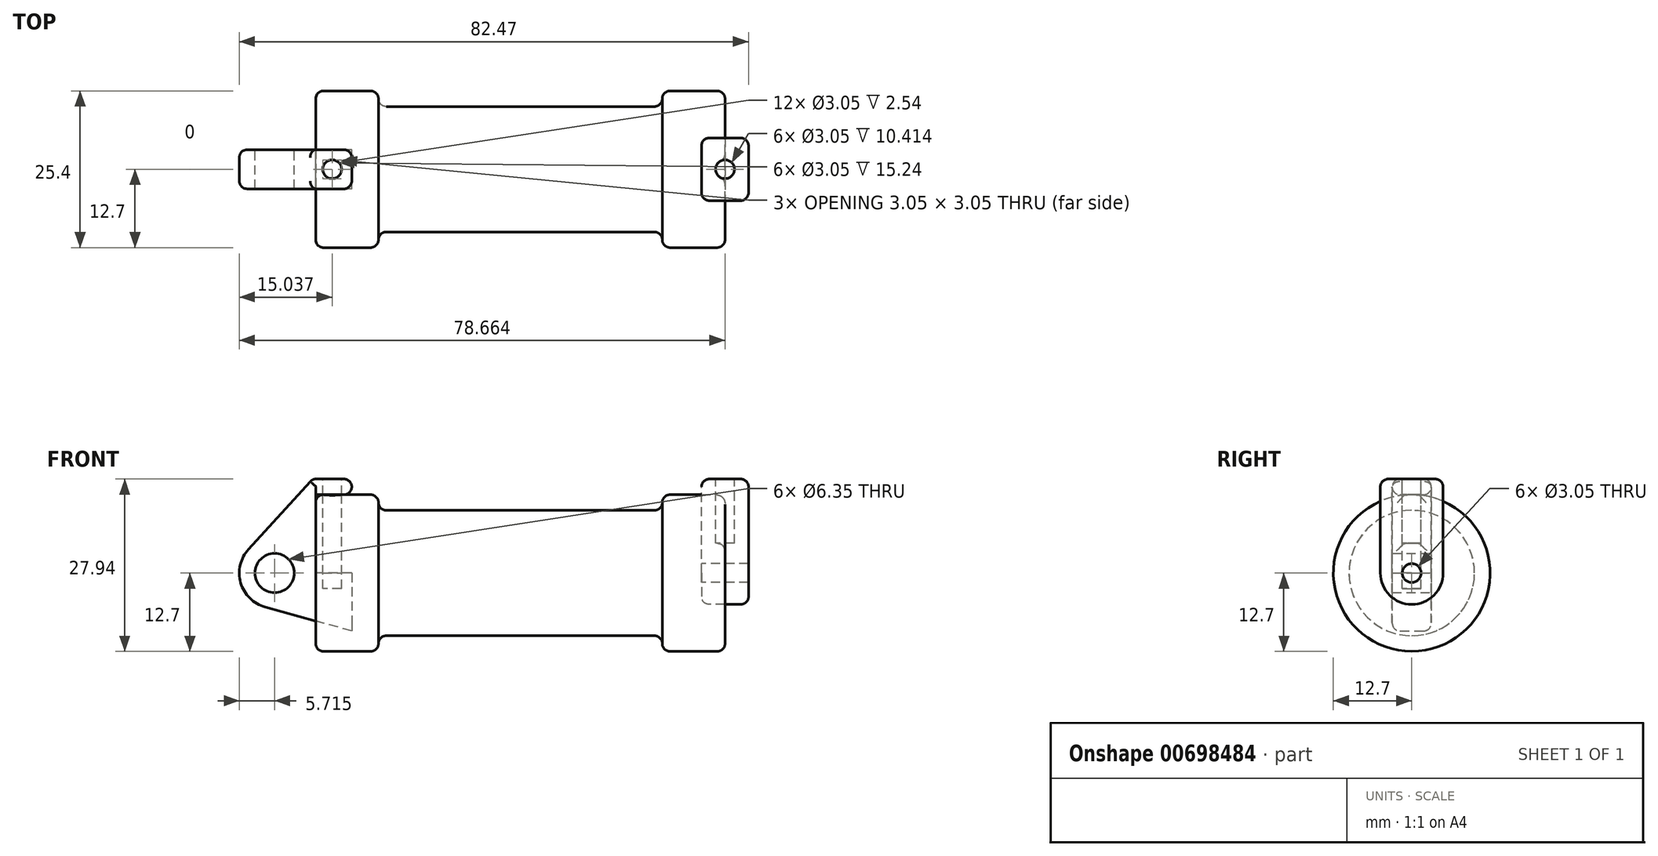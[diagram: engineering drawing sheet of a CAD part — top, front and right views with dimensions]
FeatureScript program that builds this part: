
annotation { "Feature Type Name" : "Feature", "Feature Type Description" : "" }
export const myFeature = defineFeature(function(context is Context, id is Id, definition is map)
    precondition{}
    {
        {
            var Q0;
            Q0=qCreatedBy(makeId("Front.planeOp"),FACE);
            var sketch = newSketch(context, id + "F0", { "sketchPlane" : qUnion([Q0])});
            skLineSegment(sketch, "E0", {"start": v(0, 0) * mm, "end": v(0, 12.7) * mm});
            skLineSegment(sketch, "E1", {"start": v(0, 12.7) * mm, "end": v(10.16, 12.7) * mm});
            skLineSegment(sketch, "E2", {"start": v(10.16, 12.7) * mm, "end": v(10.16, 10.16) * mm});
            skLineSegment(sketch, "E3", {"start": v(10.16, 10.16) * mm, "end": v(56.13, 10.16) * mm});
            skLineSegment(sketch, "E4", {"start": v(56.13, 10.16) * mm, "end": v(56.13, 12.7) * mm});
            skLineSegment(sketch, "E5", {"start": v(56.13, 12.7) * mm, "end": v(66.3, 12.7) * mm});
            skLineSegment(sketch, "E6", {"start": v(66.3, 12.7) * mm, "end": v(66.3, 0) * mm});
            skLineSegment(sketch, "E7", {"start": v(66.3, 0) * mm, "end": v(0, 0) * mm});
            skLineSegment(sketch, "E8", {"start": v(5.84, 15.24) * mm, "end": v(-0.5, 15.24) * mm});
            skLineSegment(sketch, "E9", {"start": v(-0.5, 15.24) * mm, "end": v(-10.88, 3.85) * mm});
            skLineSegment(sketch, "E10", {"start": v(0, 0) * mm, "end": v(-6.65, 0) * mm});
            skCircle(sketch, "E11", {"center": v(-6.65, 0) * mm, "radius": 5.72 * mm});
            skCircle(sketch, "E12", {"center": v(-6.65, 0) * mm, "radius": 3.18 * mm});
            skLineSegment(sketch, "E13", {"start": v(5.84, 15.24) * mm, "end": v(5.84, -9.4) * mm});
            skLineSegment(sketch, "E14", {"start": v(5.84, -9.4) * mm, "end": v(-8.18, -5.5) * mm});
            skSolve(sketch);
        }
        {
            var Q0;
            {var subQ1=sQuery(id+"F0.wireOp",EDGE,"E0");Q0=makeQuery(id+"F0.imprint","IMPRINT",FACE,{"disambiguationData":[TD([[makeQuery(id+"F0.imprint","IMPRINT",EDGE,{"derivedFrom":subQ1}),1.0]])]});}
            var Q1;
            {var subQ0=sQuery(id+"F0.wireOp",EDGE,"E14");Q1=makeQuery(id+"F0.imprint","IMPRINT",FACE,{"disambiguationData":[TD([[makeQuery(id+"F0.imprint","IMPRINT",EDGE,{"derivedFrom":subQ0}),-1.0]])]});}
            var Q2;
            {var subQ5=sQuery(id+"F0.wireOp",EDGE,"E12");Q2=makeQuery(id+"F0.imprint","IMPRINT",FACE,{"disambiguationData":[TD([[makeQuery(id+"F0.imprint","IMPRINT",EDGE,{"derivedFrom":subQ5}),-1.0]])]});}
            extrude(context, id + "F1", {"entities" : qUnion([Q0, Q1, Q2]), "endBound" : BoundingType.SYMMETRIC, "depth" : 6.35 * mm, "offsetDistance" : 25.4 * mm});
        }
        {
            var Q0;
            {var subQ0=sQuery(id+"F0.wireOp",EDGE,"E2");Q0=makeQuery(id+"F0.imprint","IMPRINT",FACE,{"disambiguationData":[TD([[makeQuery(id+"F0.imprint","IMPRINT",EDGE,{"derivedFrom":subQ0}),-1.0]])]});}
            var Q1;
            {var subQ0=sQuery(id+"F0.wireOp",EDGE,"E0");Q1=makeQuery(id+"F0.imprint","IMPRINT",FACE,{"disambiguationData":[TD([[makeQuery(id+"F0.imprint","IMPRINT",EDGE,{"derivedFrom":subQ0}),-1.0]])]});}
            var Q2;
            Q2=sQuery(id+"F0.wireOp",EDGE,"E7");
            revolve(context, id + "F2", {"entities" : qUnion([Q0, Q1]), "axis" : qUnion([Q2]), "revolveType" : RevolveType.FULL});
        }
        {
            var Q0;
            Q0=makeQuery(id+"F2.opRevolve","SWEPT_FACE",FACE,{"disambiguationData":[OSD([sQuery(id+"F0.wireOp",EDGE,"E6")])]});
            var sketch = newSketch(context, id + "F3", { "sketchPlane" : qUnion([Q0])});
            skCircle(sketch, "E15", {"center": v(0, 0) * mm, "radius": 1.52 * mm});
            skCircle(sketch, "E16", {"center": v(0, 0) * mm, "radius": 5.08 * mm});
            skLineSegment(sketch, "E17", {"start": v(5.08, 0) * mm, "end": v(5.08, 15.24) * mm});
            skLineSegment(sketch, "E18", {"start": v(-5.08, 0) * mm, "end": v(-5.08, 15.24) * mm});
            skLineSegment(sketch, "E19", {"start": v(-5.08, 15.24) * mm, "end": v(5.08, 15.24) * mm});
            skSolve(sketch);
        }
        {
            var Q0;
            Q0=makeQuery(id+"F3.imprint","IMPRINT",FACE,{"disambiguationData":[TD([[makeQuery(id+"F3.imprint","IMPRINT",EDGE,{"derivedFrom":sQuery(id+"F3.wireOp",EDGE,"E15")}),-1.0]])]});
            var Q1;
            {var subQ0=sQuery(id+"F3.wireOp",EDGE,"E17");var subQ1=sQuery(id+"F3.wireOp",EDGE,"E16");var subQ2=makeQuery(id+"F3.imprint","INTERSECT",VERTEX,{"derivedFrom":[subQ1,subQ0]});Q1=makeQuery(id+"F3.imprint","IMPRINT",FACE,{"disambiguationData":[TD([[makeQuery(id+"F3.imprint","IMPRINT",EDGE,{"disambiguationData":[TD([[subQ2,-1.0]])],"derivedFrom":subQ1}),-1.0]])]});}
            var Q2;
            {var subQ0=sQuery(id+"F3.wireOp",EDGE,"E19");Q2=makeQuery(id+"F3.imprint","IMPRINT",FACE,{"disambiguationData":[TD([[makeQuery(id+"F3.imprint","IMPRINT",EDGE,{"derivedFrom":subQ0}),-1.0]])]});}
            extrude(context, id + "F4", {"entities" : qUnion([Q0, Q1, Q2]), "endBound" : BoundingType.SYMMETRIC, "depth" : 7.62 * mm, "offsetDistance" : 25.4 * mm});
        }
        {
            var Q0;
            Q0=makeQuery(id+"F4.opExtrude","SWEPT_FACE",FACE,{"disambiguationData":[OSD([sQuery(id+"F3.wireOp",EDGE,"E19")])]});
            var sketch = newSketch(context, id + "F5", { "sketchPlane" : qUnion([Q0])});
            skLineSegment(sketch, "E20", {"start": v(-0.5, 3.18) * mm, "end": v(5.84, -3.18) * mm, "construction": true});
            skCircle(sketch, "E21", {"center": v(2.67, 0) * mm, "radius": 1.52 * mm});
            skLineSegment(sketch, "E22", {"start": v(70.1, 5.08) * mm, "end": v(62.48, -5.08) * mm, "construction": true});
            skCircle(sketch, "E23", {"center": v(66.3, 0) * mm, "radius": 1.52 * mm});
            skSolve(sketch);
        }
        {
            var Q0;
            Q0=makeQuery(id+"F5.imprint","IMPRINT",FACE,{"disambiguationData":[TD([[makeQuery(id+"F5.imprint","IMPRINT",EDGE,{"derivedFrom":sQuery(id+"F5.wireOp",EDGE,"E23")}),1.0]])]});
            var Q1;
            Q1=sQuery(id+"F5.wireOp",EDGE,"E21");
            var Q2;
            Q2=sQuery(id+"F5.wireOp",EDGE,"E23");
            extrude(context, id + "F6", {"entities" : qUnion([Q0]), "operationType" : NewBodyOperationType.REMOVE, "surfaceEntities" : qUnion([Q1, Q2]), "oppositeDirection" : true, "depth" : 10.4 * mm, "offsetDistance" : 25.4 * mm});
        }
        {
            var Q0;
            Q0=makeQuery(id+"F5.imprint","IMPRINT",FACE,{"disambiguationData":[TD([[makeQuery(id+"F5.imprint","IMPRINT",EDGE,{"derivedFrom":sQuery(id+"F5.wireOp",EDGE,"E21")}),1.0]])]});
            extrude(context, id + "F7", {"entities" : qUnion([Q0]), "operationType" : NewBodyOperationType.REMOVE, "oppositeDirection" : true, "depth" : 17.78 * mm, "offsetDistance" : 25.4 * mm});
        }
        {
            var Q0;
            Q0=makeQuery(id+"F2.opRevolve","SWEPT_FACE",FACE,{"disambiguationData":[OSD([sQuery(id+"F0.wireOp",EDGE,"E2")])]});
            var Q1;
            Q1=makeQuery(id+"F2.opRevolve","SWEPT_FACE",FACE,{"disambiguationData":[OSD([sQuery(id+"F0.wireOp",EDGE,"E4")])]});
            fillet(context, id + "F8", {"entities" : qUnion([Q0, Q1]), "radius" : 1.27 * mm, "tangentPropagation" : true, "allowEdgeOverflow" : false});
        }
        {
            var Q0;
            Q0=makeQuery(id+"F1.opExtrude","CAP_EDGE",EDGE,{"disambiguationData":[OSD([sQuery(id+"F0.wireOp",EDGE,"E8")])],"isStart":false});
            var Q1;
            Q1=makeQuery(id+"F1.opExtrude","SWEPT_EDGE",EDGE,{"disambiguationData":[OSD([sQuery(id+"F0.wireOp",EDGE,"E8"),sQuery(id+"F0.wireOp",EDGE,"E9")])]});
            var Q2;
            Q2=makeQuery(id+"F1.opExtrude","CAP_EDGE",EDGE,{"disambiguationData":[OSD([sQuery(id+"F0.wireOp",EDGE,"E8")])],"isStart":true});
            fillet(context, id + "F9", {"entities" : qUnion([Q0, Q1, Q2]), "radius" : 1.27 * mm, "tangentPropagation" : true, "allowEdgeOverflow" : false});
        }
        {
            var Q0;
            Q0=makeQuery(id+"F1.opExtrude","SWEPT_EDGE",EDGE,{"disambiguationData":[OSD([sQuery(id+"F0.wireOp",EDGE,"E8"),sQuery(id+"F0.wireOp",EDGE,"E13")])]});
            var Q1;
            Q1=makeQuery(id+"F1.opExtrude","CAP_EDGE",EDGE,{"disambiguationData":[OSD([sQuery(id+"F0.wireOp",EDGE,"E9")])],"isStart":true});
            var Q2;
            Q2=makeQuery(id+"F1.opExtrude","CAP_EDGE",EDGE,{"disambiguationData":[OSD([sQuery(id+"F0.wireOp",EDGE,"E9")])],"isStart":false});
            var Q3;
            {var subQ0=sQuery(id+"F0.wireOp",EDGE,"E9");Q3=makeQuery(id+"F9.opFillet","BLEND_EDGE",EDGE,{"blendedFrom":[makeQuery(id+"F1.opExtrude","SWEPT_EDGE",EDGE,{"disambiguationData":[OSD([sQuery(id+"F0.wireOp",EDGE,"E8"),subQ0])]}),makeQuery(id+"F1.opExtrude","SWEPT_FACE",FACE,{"disambiguationData":[OSD([subQ0])]})],"blendedInto":[makeQuery(id+"F1.opExtrude","SWEPT_FACE",FACE,{"disambiguationData":[OSD([subQ0])]})]});}
            var Q4;
            Q4=makeQuery(id+"F1.opExtrude","SWEPT_EDGE",EDGE,{"disambiguationData":[OSD([sQuery(id+"F0.wireOp",EDGE,"E9"),sQuery(id+"F0.wireOp",EDGE,"E11")])]});
            var Q5;
            {var subQ0=sQuery(id+"F0.wireOp",EDGE,"E5");Q5=makeQuery(id+"F8.opFillet","BLEND_EDGE",EDGE,{"blendedFrom":[makeQuery(id+"F2.opRevolve","SWEPT_EDGE",EDGE,{"disambiguationData":[OSD([sQuery(id+"F0.wireOp",EDGE,"E4"),subQ0])]}),makeQuery(id+"F2.opRevolve","SWEPT_FACE",FACE,{"disambiguationData":[OSD([subQ0])]})],"blendedInto":[makeQuery(id+"F2.opRevolve","SWEPT_FACE",FACE,{"disambiguationData":[OSD([subQ0])]})]});}
            var Q6;
            Q6=makeQuery(id+"F4.opExtrude","SWEPT_EDGE",EDGE,{"disambiguationData":[OSD([sQuery(id+"F3.wireOp",EDGE,"E17"),sQuery(id+"F3.wireOp",EDGE,"E19")])]});
            var Q7;
            Q7=makeQuery(id+"F4.opExtrude","SWEPT_EDGE",EDGE,{"disambiguationData":[OSD([sQuery(id+"F3.wireOp",EDGE,"E18"),sQuery(id+"F3.wireOp",EDGE,"E19")])]});
            var Q8;
            Q8=makeQuery(id+"F4.opExtrude","CAP_EDGE",EDGE,{"disambiguationData":[OSD([sQuery(id+"F3.wireOp",EDGE,"E19")])],"isStart":false});
            var Q9;
            Q9=makeQuery(id+"F4.opExtrude","CAP_EDGE",EDGE,{"disambiguationData":[OSD([sQuery(id+"F3.wireOp",EDGE,"E19")])],"isStart":true});
            var Q10;
            {var subQ0=sQuery(id+"F0.wireOp",EDGE,"E4");Q10=makeQuery(id+"F8.opFillet","BLEND_EDGE",EDGE,{"blendedFrom":[makeQuery(id+"F2.opRevolve","SWEPT_EDGE",EDGE,{"disambiguationData":[OSD([sQuery(id+"F0.wireOp",EDGE,"E3"),subQ0])]}),makeQuery(id+"F2.opRevolve","SWEPT_EDGE",EDGE,{"disambiguationData":[OSD([subQ0,sQuery(id+"F0.wireOp",EDGE,"E5")])]})],"blendedInto":[]});}
            var Q11;
            {var subQ0=sQuery(id+"F0.wireOp",EDGE,"E3");Q11=makeQuery(id+"F8.opFillet","BLEND_EDGE",EDGE,{"blendedFrom":[makeQuery(id+"F2.opRevolve","SWEPT_EDGE",EDGE,{"disambiguationData":[OSD([subQ0,sQuery(id+"F0.wireOp",EDGE,"E4")])]}),makeQuery(id+"F2.opRevolve","SWEPT_FACE",FACE,{"disambiguationData":[OSD([subQ0])]})],"blendedInto":[makeQuery(id+"F2.opRevolve","SWEPT_FACE",FACE,{"disambiguationData":[OSD([subQ0])]})]});}
            var Q12;
            {var subQ0=sQuery(id+"F0.wireOp",EDGE,"E1");Q12=makeQuery(id+"F8.opFillet","BLEND_EDGE",EDGE,{"blendedFrom":[makeQuery(id+"F2.opRevolve","SWEPT_EDGE",EDGE,{"disambiguationData":[OSD([subQ0,sQuery(id+"F0.wireOp",EDGE,"E2")])]}),makeQuery(id+"F2.opRevolve","SWEPT_FACE",FACE,{"disambiguationData":[OSD([subQ0])]})],"blendedInto":[makeQuery(id+"F2.opRevolve","SWEPT_FACE",FACE,{"disambiguationData":[OSD([subQ0])]})]});}
            fillet(context, id + "F10", {"entities" : qUnion([Q0, Q1, Q2, Q3, Q4, Q5, Q6, Q7, Q8, Q9, Q10, Q11, Q12]), "radius" : 1.27 * mm, "tangentPropagation" : true, "allowEdgeOverflow" : false});
        }
        {
            var Q0;
            {var subQ0=sQuery(id+"F3.wireOp",EDGE,"E19");Q0=makeQuery(id+"F10.opFillet","BLEND_EDGE",EDGE,{"blendedFrom":[makeQuery(id+"F4.opExtrude","CAP_EDGE",EDGE,{"disambiguationData":[OSD([subQ0])],"isStart":false}),makeQuery(id+"F4.opExtrude","SWEPT_FACE",FACE,{"disambiguationData":[OSD([subQ0])]})],"blendedInto":[makeQuery(id+"F4.opExtrude","SWEPT_FACE",FACE,{"disambiguationData":[OSD([subQ0])]})]});}
            var Q1;
            {var subQ0=sQuery(id+"F3.wireOp",EDGE,"E19");Q1=makeQuery(id+"F10.opFillet","BLEND_EDGE",EDGE,{"blendedFrom":[makeQuery(id+"F4.opExtrude","CAP_EDGE",EDGE,{"disambiguationData":[OSD([subQ0])],"isStart":true}),makeQuery(id+"F4.opExtrude","SWEPT_FACE",FACE,{"disambiguationData":[OSD([subQ0])]})],"blendedInto":[makeQuery(id+"F4.opExtrude","SWEPT_FACE",FACE,{"disambiguationData":[OSD([subQ0])]})]});}
            var Q2;
            {var subQ0=sQuery(id+"F3.wireOp",EDGE,"E19");Q2=makeQuery(id+"F10.opFillet","BLEND_EDGE",EDGE,{"blendedFrom":[makeQuery(id+"F4.opExtrude","SWEPT_EDGE",EDGE,{"disambiguationData":[OSD([sQuery(id+"F3.wireOp",EDGE,"E17"),subQ0])]}),makeQuery(id+"F4.opExtrude","SWEPT_FACE",FACE,{"disambiguationData":[OSD([subQ0])]})],"blendedInto":[makeQuery(id+"F4.opExtrude","SWEPT_FACE",FACE,{"disambiguationData":[OSD([subQ0])]})]});}
            var Q3;
            {var subQ0=sQuery(id+"F3.wireOp",EDGE,"E19");Q3=makeQuery(id+"F10.opFillet","BLEND_EDGE",EDGE,{"blendedFrom":[makeQuery(id+"F4.opExtrude","SWEPT_EDGE",EDGE,{"disambiguationData":[OSD([sQuery(id+"F3.wireOp",EDGE,"E18"),subQ0])]}),makeQuery(id+"F4.opExtrude","SWEPT_FACE",FACE,{"disambiguationData":[OSD([subQ0])]})],"blendedInto":[makeQuery(id+"F4.opExtrude","SWEPT_FACE",FACE,{"disambiguationData":[OSD([subQ0])]})]});}
            var Q4;
            Q4=makeQuery(id+"F4.opExtrude","CAP_EDGE",EDGE,{"disambiguationData":[OSD([sQuery(id+"F3.wireOp",EDGE,"E17")])],"isStart":false});
            var Q5;
            Q5=makeQuery(id+"F4.opExtrude","CAP_EDGE",EDGE,{"disambiguationData":[OSD([sQuery(id+"F3.wireOp",EDGE,"E18")])],"isStart":false});
            var Q6;
            Q6=makeQuery(id+"F4.opExtrude","CAP_EDGE",EDGE,{"disambiguationData":[OSD([sQuery(id+"F3.wireOp",EDGE,"E16")])],"isStart":false});
            var Q7;
            {var subQ0=sQuery(id+"F3.wireOp",EDGE,"E19");Q7=makeQuery(id+"F10.opFillet","BLEND_EDGE",EDGE,{"blendedFrom":[makeQuery(id+"F4.opExtrude","CAP_EDGE",EDGE,{"disambiguationData":[OSD([subQ0])],"isStart":false}),makeQuery(id+"F4.opExtrude","CAP_FACE",FACE,{"disambiguationData":[OSD([sQuery(id+"F3.wireOp",EDGE,"E15"),sQuery(id+"F3.wireOp",EDGE,"E16"),sQuery(id+"F3.wireOp",EDGE,"E17"),sQuery(id+"F3.wireOp",EDGE,"E18"),subQ0])],"isStart":false})],"blendedInto":[makeQuery(id+"F4.opExtrude","CAP_FACE",FACE,{"disambiguationData":[OSD([sQuery(id+"F3.wireOp",EDGE,"E15"),sQuery(id+"F3.wireOp",EDGE,"E16"),sQuery(id+"F3.wireOp",EDGE,"E17"),sQuery(id+"F3.wireOp",EDGE,"E18"),subQ0])],"isStart":false})]});}
            var Q8;
            {var subQ0=sQuery(id+"F3.wireOp",EDGE,"E19");Q8=makeQuery(id+"F10.opFillet","BLEND_EDGE",EDGE,{"blendedFrom":[makeQuery(id+"F4.opExtrude","SWEPT_EDGE",EDGE,{"disambiguationData":[OSD([sQuery(id+"F3.wireOp",EDGE,"E17"),subQ0])]}),makeQuery(id+"F4.opExtrude","CAP_EDGE",EDGE,{"disambiguationData":[OSD([subQ0])],"isStart":false})],"blendedInto":[]});}
            var Q9;
            {var subQ0=sQuery(id+"F3.wireOp",EDGE,"E19");Q9=makeQuery(id+"F10.opFillet","BLEND_EDGE",EDGE,{"blendedFrom":[makeQuery(id+"F4.opExtrude","SWEPT_EDGE",EDGE,{"disambiguationData":[OSD([sQuery(id+"F3.wireOp",EDGE,"E18"),subQ0])]}),makeQuery(id+"F4.opExtrude","CAP_EDGE",EDGE,{"disambiguationData":[OSD([subQ0])],"isStart":false})],"blendedInto":[]});}
            var Q10;
            {var subQ0=sQuery(id+"F3.wireOp",EDGE,"E18");Q10=makeQuery(id+"F10.opFillet","BLEND_EDGE",EDGE,{"blendedFrom":[makeQuery(id+"F4.opExtrude","SWEPT_EDGE",EDGE,{"disambiguationData":[OSD([subQ0,sQuery(id+"F3.wireOp",EDGE,"E19")])]}),makeQuery(id+"F4.opExtrude","SWEPT_FACE",FACE,{"disambiguationData":[OSD([subQ0])]})],"blendedInto":[makeQuery(id+"F4.opExtrude","SWEPT_FACE",FACE,{"disambiguationData":[OSD([subQ0])]})]});}
            var Q11;
            Q11=makeQuery(id+"F4.opExtrude","SWEPT_FACE",FACE,{"disambiguationData":[OSD([sQuery(id+"F3.wireOp",EDGE,"E16")])]});
            var Q12;
            Q12=makeQuery(id+"F2.opRevolve","SWEPT_EDGE",EDGE,{"disambiguationData":[OSD([sQuery(id+"F0.wireOp",EDGE,"E0"),sQuery(id+"F0.wireOp",EDGE,"E1")])]});
            var Q13;
            {var subQ0=sQuery(id+"F0.wireOp",EDGE,"E9");Q13=makeQuery(id+"F10.opFillet","BLEND_EDGE",EDGE,{"blendedFrom":[makeQuery(id+"F1.opExtrude","CAP_EDGE",EDGE,{"disambiguationData":[OSD([subQ0])],"isStart":true}),makeQuery(id+"F1.opExtrude","SWEPT_FACE",FACE,{"disambiguationData":[OSD([subQ0])]})],"blendedInto":[makeQuery(id+"F1.opExtrude","SWEPT_FACE",FACE,{"disambiguationData":[OSD([subQ0])]})]});}
            var Q14;
            {var subQ0=sQuery(id+"F0.wireOp",EDGE,"E9");Q14=makeQuery(id+"F10.opFillet","BLEND_EDGE",EDGE,{"blendedFrom":[makeQuery(id+"F1.opExtrude","CAP_EDGE",EDGE,{"disambiguationData":[OSD([subQ0])],"isStart":false}),makeQuery(id+"F1.opExtrude","CAP_FACE",FACE,{"disambiguationData":[OSD([sQuery(id+"F0.wireOp",EDGE,"E0"),sQuery(id+"F0.wireOp",EDGE,"E1"),sQuery(id+"F0.wireOp",EDGE,"E7"),sQuery(id+"F0.wireOp",EDGE,"E8"),subQ0,sQuery(id+"F0.wireOp",EDGE,"E11"),sQuery(id+"F0.wireOp",EDGE,"E12"),sQuery(id+"F0.wireOp",EDGE,"E13"),sQuery(id+"F0.wireOp",EDGE,"E14")])],"isStart":false})],"blendedInto":[makeQuery(id+"F1.opExtrude","CAP_FACE",FACE,{"disambiguationData":[OSD([sQuery(id+"F0.wireOp",EDGE,"E0"),sQuery(id+"F0.wireOp",EDGE,"E1"),sQuery(id+"F0.wireOp",EDGE,"E7"),sQuery(id+"F0.wireOp",EDGE,"E8"),subQ0,sQuery(id+"F0.wireOp",EDGE,"E11"),sQuery(id+"F0.wireOp",EDGE,"E12"),sQuery(id+"F0.wireOp",EDGE,"E13"),sQuery(id+"F0.wireOp",EDGE,"E14")])],"isStart":false})]});}
            var Q15;
            Q15=makeQuery(id+"F2.opRevolve","SWEPT_FACE",FACE,{"disambiguationData":[OSD([sQuery(id+"F0.wireOp",EDGE,"E6")])]});
            var Q16;
            {var subQ0=sQuery(id+"F0.wireOp",EDGE,"E5");Q16=makeQuery(id+"F8.opFillet","BLEND_EDGE",EDGE,{"blendedFrom":[makeQuery(id+"F2.opRevolve","SWEPT_EDGE",EDGE,{"disambiguationData":[OSD([sQuery(id+"F0.wireOp",EDGE,"E4"),subQ0])]}),makeQuery(id+"F2.opRevolve","SWEPT_FACE",FACE,{"disambiguationData":[OSD([subQ0])]})],"blendedInto":[makeQuery(id+"F2.opRevolve","SWEPT_FACE",FACE,{"disambiguationData":[OSD([subQ0])]})]});}
            var Q17;
            {var subQ0=sQuery(id+"F0.wireOp",EDGE,"E11");Q17=makeQuery(id+"F10.opFillet","BLEND_EDGE",EDGE,{"blendedFrom":[makeQuery(id+"F1.opExtrude","CAP_EDGE",EDGE,{"disambiguationData":[OSD([subQ0])],"isStart":false}),makeQuery(id+"F1.opExtrude","SWEPT_FACE",FACE,{"disambiguationData":[OSD([subQ0])]})],"blendedInto":[makeQuery(id+"F1.opExtrude","SWEPT_FACE",FACE,{"disambiguationData":[OSD([subQ0])]})]});}
            var Q18;
            {var subQ0=sQuery(id+"F0.wireOp",EDGE,"E11");Q18=makeQuery(id+"F10.opFillet","BLEND_EDGE",EDGE,{"blendedFrom":[makeQuery(id+"F1.opExtrude","CAP_EDGE",EDGE,{"disambiguationData":[OSD([subQ0])],"isStart":false}),makeQuery(id+"F1.opExtrude","CAP_FACE",FACE,{"disambiguationData":[OSD([sQuery(id+"F0.wireOp",EDGE,"E0"),sQuery(id+"F0.wireOp",EDGE,"E1"),sQuery(id+"F0.wireOp",EDGE,"E7"),sQuery(id+"F0.wireOp",EDGE,"E8"),sQuery(id+"F0.wireOp",EDGE,"E9"),subQ0,sQuery(id+"F0.wireOp",EDGE,"E12"),sQuery(id+"F0.wireOp",EDGE,"E13"),sQuery(id+"F0.wireOp",EDGE,"E14")])],"isStart":false})],"blendedInto":[makeQuery(id+"F1.opExtrude","CAP_FACE",FACE,{"disambiguationData":[OSD([sQuery(id+"F0.wireOp",EDGE,"E0"),sQuery(id+"F0.wireOp",EDGE,"E1"),sQuery(id+"F0.wireOp",EDGE,"E7"),sQuery(id+"F0.wireOp",EDGE,"E8"),sQuery(id+"F0.wireOp",EDGE,"E9"),subQ0,sQuery(id+"F0.wireOp",EDGE,"E12"),sQuery(id+"F0.wireOp",EDGE,"E13"),sQuery(id+"F0.wireOp",EDGE,"E14")])],"isStart":false})]});}
            var Q19;
            {var subQ0=sQuery(id+"F0.wireOp",EDGE,"E14");Q19=makeQuery(id+"F10.opFillet","BLEND_EDGE",EDGE,{"blendedFrom":[makeQuery(id+"F1.opExtrude","CAP_EDGE",EDGE,{"disambiguationData":[OSD([subQ0])],"isStart":false}),makeQuery(id+"F1.opExtrude","CAP_FACE",FACE,{"disambiguationData":[OSD([sQuery(id+"F0.wireOp",EDGE,"E0"),sQuery(id+"F0.wireOp",EDGE,"E1"),sQuery(id+"F0.wireOp",EDGE,"E7"),sQuery(id+"F0.wireOp",EDGE,"E8"),sQuery(id+"F0.wireOp",EDGE,"E9"),sQuery(id+"F0.wireOp",EDGE,"E11"),sQuery(id+"F0.wireOp",EDGE,"E12"),sQuery(id+"F0.wireOp",EDGE,"E13"),subQ0])],"isStart":false})],"blendedInto":[makeQuery(id+"F1.opExtrude","CAP_FACE",FACE,{"disambiguationData":[OSD([sQuery(id+"F0.wireOp",EDGE,"E0"),sQuery(id+"F0.wireOp",EDGE,"E1"),sQuery(id+"F0.wireOp",EDGE,"E7"),sQuery(id+"F0.wireOp",EDGE,"E8"),sQuery(id+"F0.wireOp",EDGE,"E9"),sQuery(id+"F0.wireOp",EDGE,"E11"),sQuery(id+"F0.wireOp",EDGE,"E12"),sQuery(id+"F0.wireOp",EDGE,"E13"),subQ0])],"isStart":false})]});}
            var Q20;
            Q20=makeQuery(id+"F10.opFillet","BLEND_EDGE",EDGE,{"blendedFrom":[makeQuery(id+"F1.opExtrude","CAP_EDGE",EDGE,{"disambiguationData":[OSD([sQuery(id+"F0.wireOp",EDGE,"E11")])],"isStart":false}),makeQuery(id+"F1.opExtrude","CAP_EDGE",EDGE,{"disambiguationData":[OSD([sQuery(id+"F0.wireOp",EDGE,"E14")])],"isStart":false})],"blendedInto":[]});
            var Q21;
            {var subQ0=sQuery(id+"F0.wireOp",EDGE,"E14");Q21=makeQuery(id+"F10.opFillet","BLEND_EDGE",EDGE,{"blendedFrom":[makeQuery(id+"F1.opExtrude","CAP_EDGE",EDGE,{"disambiguationData":[OSD([subQ0])],"isStart":false}),makeQuery(id+"F1.opExtrude","SWEPT_FACE",FACE,{"disambiguationData":[OSD([subQ0])]})],"blendedInto":[makeQuery(id+"F1.opExtrude","SWEPT_FACE",FACE,{"disambiguationData":[OSD([subQ0])]})]});}
            var Q22;
            {var subQ0=sQuery(id+"F0.wireOp",EDGE,"E11");Q22=makeQuery(id+"F10.opFillet","BLEND_EDGE",EDGE,{"blendedFrom":[makeQuery(id+"F1.opExtrude","CAP_EDGE",EDGE,{"disambiguationData":[OSD([subQ0])],"isStart":true}),makeQuery(id+"F1.opExtrude","SWEPT_FACE",FACE,{"disambiguationData":[OSD([subQ0])]})],"blendedInto":[makeQuery(id+"F1.opExtrude","SWEPT_FACE",FACE,{"disambiguationData":[OSD([subQ0])]})]});}
            var Q23;
            Q23=makeQuery(id+"F1.opExtrude","SWEPT_EDGE",EDGE,{"disambiguationData":[OSD([sQuery(id+"F0.wireOp",EDGE,"E11"),sQuery(id+"F0.wireOp",EDGE,"E14")])]});
            var Q24;
            {var subQ0=sQuery(id+"F0.wireOp",EDGE,"E14");Q24=makeQuery(id+"F10.opFillet","BLEND_EDGE",EDGE,{"blendedFrom":[makeQuery(id+"F1.opExtrude","CAP_EDGE",EDGE,{"disambiguationData":[OSD([subQ0])],"isStart":true}),makeQuery(id+"F1.opExtrude","SWEPT_FACE",FACE,{"disambiguationData":[OSD([subQ0])]})],"blendedInto":[makeQuery(id+"F1.opExtrude","SWEPT_FACE",FACE,{"disambiguationData":[OSD([subQ0])]})]});}
            var Q25;
            {var subQ0=sQuery(id+"F0.wireOp",EDGE,"E9");Q25=makeQuery(id+"F10.opFillet","BLEND_EDGE",EDGE,{"blendedFrom":[makeQuery(id+"F1.opExtrude","CAP_EDGE",EDGE,{"disambiguationData":[OSD([subQ0])],"isStart":true}),makeQuery(id+"F1.opExtrude","CAP_FACE",FACE,{"disambiguationData":[OSD([sQuery(id+"F0.wireOp",EDGE,"E0"),sQuery(id+"F0.wireOp",EDGE,"E1"),sQuery(id+"F0.wireOp",EDGE,"E7"),sQuery(id+"F0.wireOp",EDGE,"E8"),subQ0,sQuery(id+"F0.wireOp",EDGE,"E11"),sQuery(id+"F0.wireOp",EDGE,"E12"),sQuery(id+"F0.wireOp",EDGE,"E13"),sQuery(id+"F0.wireOp",EDGE,"E14")])],"isStart":true})],"blendedInto":[makeQuery(id+"F1.opExtrude","CAP_FACE",FACE,{"disambiguationData":[OSD([sQuery(id+"F0.wireOp",EDGE,"E0"),sQuery(id+"F0.wireOp",EDGE,"E1"),sQuery(id+"F0.wireOp",EDGE,"E7"),sQuery(id+"F0.wireOp",EDGE,"E8"),subQ0,sQuery(id+"F0.wireOp",EDGE,"E11"),sQuery(id+"F0.wireOp",EDGE,"E12"),sQuery(id+"F0.wireOp",EDGE,"E13"),sQuery(id+"F0.wireOp",EDGE,"E14")])],"isStart":true})]});}
            var Q26;
            {var subQ0=sQuery(id+"F0.wireOp",EDGE,"E8");Q26=makeQuery(id+"F9.opFillet","BLEND_EDGE",EDGE,{"blendedFrom":[makeQuery(id+"F1.opExtrude","CAP_EDGE",EDGE,{"disambiguationData":[OSD([subQ0])],"isStart":true}),makeQuery(id+"F1.opExtrude","CAP_FACE",FACE,{"disambiguationData":[OSD([sQuery(id+"F0.wireOp",EDGE,"E0"),sQuery(id+"F0.wireOp",EDGE,"E1"),sQuery(id+"F0.wireOp",EDGE,"E7"),subQ0,sQuery(id+"F0.wireOp",EDGE,"E9"),sQuery(id+"F0.wireOp",EDGE,"E11"),sQuery(id+"F0.wireOp",EDGE,"E12"),sQuery(id+"F0.wireOp",EDGE,"E13"),sQuery(id+"F0.wireOp",EDGE,"E14")])],"isStart":true})],"blendedInto":[makeQuery(id+"F1.opExtrude","CAP_FACE",FACE,{"disambiguationData":[OSD([sQuery(id+"F0.wireOp",EDGE,"E0"),sQuery(id+"F0.wireOp",EDGE,"E1"),sQuery(id+"F0.wireOp",EDGE,"E7"),subQ0,sQuery(id+"F0.wireOp",EDGE,"E9"),sQuery(id+"F0.wireOp",EDGE,"E11"),sQuery(id+"F0.wireOp",EDGE,"E12"),sQuery(id+"F0.wireOp",EDGE,"E13"),sQuery(id+"F0.wireOp",EDGE,"E14")])],"isStart":true})]});}
            var Q27;
            {var subQ0=sQuery(id+"F0.wireOp",EDGE,"E13");var subQ1=sQuery(id+"F0.wireOp",EDGE,"E8");var subQ2=sQuery(id+"F0.wireOp",EDGE,"E1");Q27=makeQuery(id+"F10.opFillet","BLEND_EDGE",EDGE,{"blendedFrom":[makeQuery(id+"F1.opExtrude","CAP_EDGE",EDGE,{"disambiguationData":[OSD([subQ0]),TDD([makeQuery(id+"F0.imprint","IMPRINT",EDGE,{"disambiguationData":[TD([[makeQuery(id+"F0.imprint","INTERSECT",VERTEX,{"derivedFrom":[subQ1,subQ0]}),-1.0]])],"derivedFrom":subQ0})])],"isStart":true}),makeQuery(id+"F1.opExtrude","CAP_FACE",FACE,{"disambiguationData":[OSD([sQuery(id+"F0.wireOp",EDGE,"E0"),subQ2,sQuery(id+"F0.wireOp",EDGE,"E7"),subQ1,sQuery(id+"F0.wireOp",EDGE,"E9"),sQuery(id+"F0.wireOp",EDGE,"E11"),sQuery(id+"F0.wireOp",EDGE,"E12"),subQ0,sQuery(id+"F0.wireOp",EDGE,"E14")])],"isStart":true})],"blendedInto":[makeQuery(id+"F1.opExtrude","CAP_FACE",FACE,{"disambiguationData":[OSD([sQuery(id+"F0.wireOp",EDGE,"E0"),subQ2,sQuery(id+"F0.wireOp",EDGE,"E7"),subQ1,sQuery(id+"F0.wireOp",EDGE,"E9"),sQuery(id+"F0.wireOp",EDGE,"E11"),sQuery(id+"F0.wireOp",EDGE,"E12"),subQ0,sQuery(id+"F0.wireOp",EDGE,"E14")])],"isStart":true})]});}
            var Q28;
            {var subQ0=sQuery(id+"F0.wireOp",EDGE,"E13");var subQ1=sQuery(id+"F0.wireOp",EDGE,"E8");var subQ2=makeQuery(id+"F0.imprint","IMPRINT",EDGE,{"disambiguationData":[TD([[makeQuery(id+"F0.imprint","INTERSECT",VERTEX,{"derivedFrom":[subQ1,subQ0]}),-1.0]])],"derivedFrom":subQ0});Q28=makeQuery(id+"F10.opFillet","BLEND_EDGE",EDGE,{"blendedFrom":[makeQuery(id+"F9.opFillet","BLEND_EDGE",EDGE,{"blendedFrom":[makeQuery(id+"F1.opExtrude","CAP_EDGE",EDGE,{"disambiguationData":[OSD([subQ1])],"isStart":true}),makeQuery(id+"F1.opExtrude","SWEPT_FACE",FACE,{"disambiguationData":[OSD([subQ0]),TDD([subQ2])]})],"blendedInto":[makeQuery(id+"F1.opExtrude","SWEPT_FACE",FACE,{"disambiguationData":[OSD([subQ0]),TDD([subQ2])]})]}),makeQuery(id+"F1.opExtrude","CAP_EDGE",EDGE,{"disambiguationData":[OSD([subQ0]),TDD([subQ2])],"isStart":true})],"blendedInto":[]});}
            var Q29;
            {var subQ0=sQuery(id+"F0.wireOp",EDGE,"E1");var subQ1=sQuery(id+"F0.wireOp",EDGE,"E13");Q29=makeQuery(id+"F10.opFillet","BLEND_EDGE",EDGE,{"blendedFrom":[makeQuery(id+"F1.opExtrude","CAP_EDGE",EDGE,{"disambiguationData":[OSD([subQ1]),TDD([makeQuery(id+"F0.imprint","IMPRINT",EDGE,{"disambiguationData":[TD([[makeQuery(id+"F0.imprint","INTERSECT",VERTEX,{"derivedFrom":[sQuery(id+"F0.wireOp",EDGE,"E8"),subQ1]}),-1.0]])],"derivedFrom":subQ1})])],"isStart":true}),makeQuery(id+"F1.opExtrude","SWEPT_FACE",FACE,{"disambiguationData":[OSD([subQ0])]})],"blendedInto":[makeQuery(id+"F1.opExtrude","SWEPT_FACE",FACE,{"disambiguationData":[OSD([subQ0])]})]});}
            var Q30;
            Q30=makeQuery(id+"F1.opExtrude","CAP_EDGE",EDGE,{"disambiguationData":[OSD([sQuery(id+"F0.wireOp",EDGE,"E1")])],"isStart":true});
            var Q31;
            {var subQ0=sQuery(id+"F0.wireOp",EDGE,"E11");Q31=makeQuery(id+"F10.opFillet","BLEND_EDGE",EDGE,{"blendedFrom":[makeQuery(id+"F1.opExtrude","CAP_EDGE",EDGE,{"disambiguationData":[OSD([subQ0])],"isStart":true}),makeQuery(id+"F1.opExtrude","CAP_FACE",FACE,{"disambiguationData":[OSD([sQuery(id+"F0.wireOp",EDGE,"E0"),sQuery(id+"F0.wireOp",EDGE,"E1"),sQuery(id+"F0.wireOp",EDGE,"E7"),sQuery(id+"F0.wireOp",EDGE,"E8"),sQuery(id+"F0.wireOp",EDGE,"E9"),subQ0,sQuery(id+"F0.wireOp",EDGE,"E12"),sQuery(id+"F0.wireOp",EDGE,"E13"),sQuery(id+"F0.wireOp",EDGE,"E14")])],"isStart":true})],"blendedInto":[makeQuery(id+"F1.opExtrude","CAP_FACE",FACE,{"disambiguationData":[OSD([sQuery(id+"F0.wireOp",EDGE,"E0"),sQuery(id+"F0.wireOp",EDGE,"E1"),sQuery(id+"F0.wireOp",EDGE,"E7"),sQuery(id+"F0.wireOp",EDGE,"E8"),sQuery(id+"F0.wireOp",EDGE,"E9"),subQ0,sQuery(id+"F0.wireOp",EDGE,"E12"),sQuery(id+"F0.wireOp",EDGE,"E13"),sQuery(id+"F0.wireOp",EDGE,"E14")])],"isStart":true})]});}
            var Q32;
            {var subQ0=sQuery(id+"F0.wireOp",EDGE,"E14");Q32=makeQuery(id+"F10.opFillet","BLEND_EDGE",EDGE,{"blendedFrom":[makeQuery(id+"F1.opExtrude","CAP_EDGE",EDGE,{"disambiguationData":[OSD([subQ0])],"isStart":true}),makeQuery(id+"F1.opExtrude","CAP_FACE",FACE,{"disambiguationData":[OSD([sQuery(id+"F0.wireOp",EDGE,"E0"),sQuery(id+"F0.wireOp",EDGE,"E1"),sQuery(id+"F0.wireOp",EDGE,"E7"),sQuery(id+"F0.wireOp",EDGE,"E8"),sQuery(id+"F0.wireOp",EDGE,"E9"),sQuery(id+"F0.wireOp",EDGE,"E11"),sQuery(id+"F0.wireOp",EDGE,"E12"),sQuery(id+"F0.wireOp",EDGE,"E13"),subQ0])],"isStart":true})],"blendedInto":[makeQuery(id+"F1.opExtrude","CAP_FACE",FACE,{"disambiguationData":[OSD([sQuery(id+"F0.wireOp",EDGE,"E0"),sQuery(id+"F0.wireOp",EDGE,"E1"),sQuery(id+"F0.wireOp",EDGE,"E7"),sQuery(id+"F0.wireOp",EDGE,"E8"),sQuery(id+"F0.wireOp",EDGE,"E9"),sQuery(id+"F0.wireOp",EDGE,"E11"),sQuery(id+"F0.wireOp",EDGE,"E12"),sQuery(id+"F0.wireOp",EDGE,"E13"),subQ0])],"isStart":true})]});}
            var Q33;
            {var subQ0=sQuery(id+"F0.wireOp",EDGE,"E4");Q33=makeQuery(id+"F8.opFillet","BLEND_EDGE",EDGE,{"blendedFrom":[makeQuery(id+"F2.opRevolve","SWEPT_EDGE",EDGE,{"disambiguationData":[OSD([sQuery(id+"F0.wireOp",EDGE,"E3"),subQ0])]}),makeQuery(id+"F2.opRevolve","SWEPT_EDGE",EDGE,{"disambiguationData":[OSD([subQ0,sQuery(id+"F0.wireOp",EDGE,"E5")])]})],"blendedInto":[]});}
            var Q34;
            Q34=makeQuery(id+"F2.opRevolve","SWEPT_FACE",FACE,{"disambiguationData":[OSD([sQuery(id+"F0.wireOp",EDGE,"E3")])]});
            var Q35;
            {var subQ0=sQuery(id+"F0.wireOp",EDGE,"E1");Q35=makeQuery(id+"F8.opFillet","BLEND_EDGE",EDGE,{"blendedFrom":[makeQuery(id+"F2.opRevolve","SWEPT_EDGE",EDGE,{"disambiguationData":[OSD([subQ0,sQuery(id+"F0.wireOp",EDGE,"E2")])]}),makeQuery(id+"F2.opRevolve","SWEPT_FACE",FACE,{"disambiguationData":[OSD([subQ0])]})],"blendedInto":[makeQuery(id+"F2.opRevolve","SWEPT_FACE",FACE,{"disambiguationData":[OSD([subQ0])]})]});}
            var Q36;
            {var subQ0=sQuery(id+"F0.wireOp",EDGE,"E3");Q36=makeQuery(id+"F8.opFillet","BLEND_EDGE",EDGE,{"blendedFrom":[makeQuery(id+"F2.opRevolve","SWEPT_EDGE",EDGE,{"disambiguationData":[OSD([sQuery(id+"F0.wireOp",EDGE,"E2"),subQ0])]}),makeQuery(id+"F2.opRevolve","SWEPT_FACE",FACE,{"disambiguationData":[OSD([subQ0])]})],"blendedInto":[makeQuery(id+"F2.opRevolve","SWEPT_FACE",FACE,{"disambiguationData":[OSD([subQ0])]})]});}
            var Q37;
            Q37=makeQuery(id+"F8.opFillet","BLEND_FACE",FACE,{"disambiguationData":[OSD([sQuery(id+"F0.wireOp",EDGE,"E1"),sQuery(id+"F0.wireOp",EDGE,"E2")])]});
            var Q38;
            Q38=makeQuery(id+"F4.opExtrude","CAP_EDGE",EDGE,{"disambiguationData":[OSD([sQuery(id+"F3.wireOp",EDGE,"E18")])],"isStart":true});
            var Q39;
            {var subQ0=sQuery(id+"F3.wireOp",EDGE,"E19");Q39=makeQuery(id+"F10.opFillet","BLEND_EDGE",EDGE,{"blendedFrom":[makeQuery(id+"F4.opExtrude","CAP_EDGE",EDGE,{"disambiguationData":[OSD([subQ0])],"isStart":true}),makeQuery(id+"F4.opExtrude","CAP_FACE",FACE,{"disambiguationData":[OSD([sQuery(id+"F3.wireOp",EDGE,"E15"),sQuery(id+"F3.wireOp",EDGE,"E16"),sQuery(id+"F3.wireOp",EDGE,"E17"),sQuery(id+"F3.wireOp",EDGE,"E18"),subQ0])],"isStart":true})],"blendedInto":[makeQuery(id+"F4.opExtrude","CAP_FACE",FACE,{"disambiguationData":[OSD([sQuery(id+"F3.wireOp",EDGE,"E15"),sQuery(id+"F3.wireOp",EDGE,"E16"),sQuery(id+"F3.wireOp",EDGE,"E17"),sQuery(id+"F3.wireOp",EDGE,"E18"),subQ0])],"isStart":true})]});}
            var Q40;
            {var subQ0=sQuery(id+"F3.wireOp",EDGE,"E19");Q40=makeQuery(id+"F10.opFillet","BLEND_EDGE",EDGE,{"blendedFrom":[makeQuery(id+"F4.opExtrude","SWEPT_EDGE",EDGE,{"disambiguationData":[OSD([sQuery(id+"F3.wireOp",EDGE,"E17"),subQ0])]}),makeQuery(id+"F4.opExtrude","CAP_EDGE",EDGE,{"disambiguationData":[OSD([subQ0])],"isStart":true})],"blendedInto":[]});}
            var Q41;
            {var subQ0=sQuery(id+"F3.wireOp",EDGE,"E19");Q41=makeQuery(id+"F10.opFillet","BLEND_EDGE",EDGE,{"blendedFrom":[makeQuery(id+"F4.opExtrude","SWEPT_EDGE",EDGE,{"disambiguationData":[OSD([sQuery(id+"F3.wireOp",EDGE,"E18"),subQ0])]}),makeQuery(id+"F4.opExtrude","CAP_EDGE",EDGE,{"disambiguationData":[OSD([subQ0])],"isStart":true})],"blendedInto":[]});}
            var Q42;
            Q42=makeQuery(id+"F4.opExtrude","CAP_EDGE",EDGE,{"disambiguationData":[OSD([sQuery(id+"F3.wireOp",EDGE,"E17")])],"isStart":true});
            var Q43;
            {var subQ0=sQuery(id+"F3.wireOp",EDGE,"E17");Q43=makeQuery(id+"F10.opFillet","BLEND_EDGE",EDGE,{"blendedFrom":[makeQuery(id+"F4.opExtrude","SWEPT_EDGE",EDGE,{"disambiguationData":[OSD([subQ0,sQuery(id+"F3.wireOp",EDGE,"E19")])]}),makeQuery(id+"F4.opExtrude","SWEPT_FACE",FACE,{"disambiguationData":[OSD([subQ0])]})],"blendedInto":[makeQuery(id+"F4.opExtrude","SWEPT_FACE",FACE,{"disambiguationData":[OSD([subQ0])]})]});}
            var Q44;
            {var subQ0=sQuery(id+"F0.wireOp",EDGE,"E8");var subQ1=makeQuery(id+"F1.opExtrude","CAP_EDGE",EDGE,{"disambiguationData":[OSD([subQ0])],"isStart":true});Q44=makeQuery(id+"F10.opFillet","BLEND_EDGE",EDGE,{"blendedFrom":[makeQuery(id+"F9.opFillet","BLEND_EDGE",EDGE,{"blendedFrom":[makeQuery(id+"F1.opExtrude","SWEPT_EDGE",EDGE,{"disambiguationData":[OSD([subQ0,sQuery(id+"F0.wireOp",EDGE,"E9")])]}),subQ1],"blendedInto":[]}),makeQuery(id+"F9.opFillet","BLEND_FACE",FACE,{"disambiguationData":[OSD([subQ0]),TDD([subQ1])]})],"blendedInto":[makeQuery(id+"F9.opFillet","BLEND_FACE",FACE,{"disambiguationData":[OSD([subQ0]),TDD([subQ1])]})]});}
            var Q45;
            {var subQ0=sQuery(id+"F0.wireOp",EDGE,"E8");Q45=makeQuery(id+"F10.opFillet","BLEND_EDGE",EDGE,{"blendedFrom":[makeQuery(id+"F1.opExtrude","SWEPT_EDGE",EDGE,{"disambiguationData":[OSD([subQ0,sQuery(id+"F0.wireOp",EDGE,"E13")])]}),makeQuery(id+"F1.opExtrude","SWEPT_FACE",FACE,{"disambiguationData":[OSD([subQ0])]})],"blendedInto":[makeQuery(id+"F1.opExtrude","SWEPT_FACE",FACE,{"disambiguationData":[OSD([subQ0])]})]});}
            var Q46;
            {var subQ0=sQuery(id+"F0.wireOp",EDGE,"E8");var subQ1=makeQuery(id+"F1.opExtrude","CAP_EDGE",EDGE,{"disambiguationData":[OSD([subQ0])],"isStart":true});var subQ2=sQuery(id+"F0.wireOp",EDGE,"E13");Q46=makeQuery(id+"F10.opFillet","BLEND_EDGE",EDGE,{"blendedFrom":[makeQuery(id+"F9.opFillet","BLEND_EDGE",EDGE,{"blendedFrom":[subQ1,makeQuery(id+"F1.opExtrude","SWEPT_FACE",FACE,{"disambiguationData":[OSD([subQ2]),TDD([makeQuery(id+"F0.imprint","IMPRINT",EDGE,{"disambiguationData":[TD([[makeQuery(id+"F0.imprint","INTERSECT",VERTEX,{"derivedFrom":[subQ0,subQ2]}),-1.0]])],"derivedFrom":subQ2})])]})],"blendedInto":[makeQuery(id+"F1.opExtrude","SWEPT_FACE",FACE,{"disambiguationData":[OSD([subQ2]),TDD([makeQuery(id+"F0.imprint","IMPRINT",EDGE,{"disambiguationData":[TD([[makeQuery(id+"F0.imprint","INTERSECT",VERTEX,{"derivedFrom":[subQ0,subQ2]}),-1.0]])],"derivedFrom":subQ2})])]})]}),makeQuery(id+"F9.opFillet","BLEND_FACE",FACE,{"disambiguationData":[OSD([subQ0]),TDD([subQ1])]})],"blendedInto":[makeQuery(id+"F9.opFillet","BLEND_FACE",FACE,{"disambiguationData":[OSD([subQ0]),TDD([subQ1])]})]});}
            var Q47;
            {var subQ0=sQuery(id+"F0.wireOp",EDGE,"E13");var subQ1=sQuery(id+"F0.wireOp",EDGE,"E8");Q47=makeQuery(id+"F10.opFillet","BLEND_EDGE",EDGE,{"blendedFrom":[makeQuery(id+"F1.opExtrude","SWEPT_EDGE",EDGE,{"disambiguationData":[OSD([subQ1,subQ0])]}),makeQuery(id+"F9.opFillet","BLEND_EDGE",EDGE,{"blendedFrom":[makeQuery(id+"F1.opExtrude","CAP_EDGE",EDGE,{"disambiguationData":[OSD([subQ1])],"isStart":true}),makeQuery(id+"F1.opExtrude","SWEPT_FACE",FACE,{"disambiguationData":[OSD([subQ0]),TDD([makeQuery(id+"F0.imprint","IMPRINT",EDGE,{"disambiguationData":[TD([[makeQuery(id+"F0.imprint","INTERSECT",VERTEX,{"derivedFrom":[subQ1,subQ0]}),-1.0]])],"derivedFrom":subQ0})])]})],"blendedInto":[makeQuery(id+"F1.opExtrude","SWEPT_FACE",FACE,{"disambiguationData":[OSD([subQ0]),TDD([makeQuery(id+"F0.imprint","IMPRINT",EDGE,{"disambiguationData":[TD([[makeQuery(id+"F0.imprint","INTERSECT",VERTEX,{"derivedFrom":[subQ1,subQ0]}),-1.0]])],"derivedFrom":subQ0})])]})]})],"blendedInto":[]});}
            var Q48;
            {var subQ0=sQuery(id+"F0.wireOp",EDGE,"E8");Q48=makeQuery(id+"F9.opFillet","BLEND_EDGE",EDGE,{"blendedFrom":[makeQuery(id+"F1.opExtrude","CAP_EDGE",EDGE,{"disambiguationData":[OSD([subQ0])],"isStart":true}),makeQuery(id+"F1.opExtrude","SWEPT_FACE",FACE,{"disambiguationData":[OSD([subQ0])]})],"blendedInto":[makeQuery(id+"F1.opExtrude","SWEPT_FACE",FACE,{"disambiguationData":[OSD([subQ0])]})]});}
            var Q49;
            {var subQ0=sQuery(id+"F0.wireOp",EDGE,"E9");var subQ1=sQuery(id+"F0.wireOp",EDGE,"E8");Q49=makeQuery(id+"F10.opFillet","BLEND_EDGE",EDGE,{"blendedFrom":[makeQuery(id+"F9.opFillet","BLEND_EDGE",EDGE,{"blendedFrom":[makeQuery(id+"F1.opExtrude","SWEPT_EDGE",EDGE,{"disambiguationData":[OSD([subQ1,subQ0])]}),makeQuery(id+"F1.opExtrude","CAP_EDGE",EDGE,{"disambiguationData":[OSD([subQ1])],"isStart":true})],"blendedInto":[]}),makeQuery(id+"F9.opFillet","BLEND_FACE",FACE,{"disambiguationData":[OSD([subQ1,subQ0])]})],"blendedInto":[makeQuery(id+"F9.opFillet","BLEND_FACE",FACE,{"disambiguationData":[OSD([subQ1,subQ0])]})]});}
            var Q50;
            {var subQ0=sQuery(id+"F0.wireOp",EDGE,"E9");var subQ1=sQuery(id+"F0.wireOp",EDGE,"E8");Q50=makeQuery(id+"F10.opFillet","BLEND_EDGE",EDGE,{"blendedFrom":[makeQuery(id+"F9.opFillet","BLEND_EDGE",EDGE,{"blendedFrom":[makeQuery(id+"F1.opExtrude","SWEPT_EDGE",EDGE,{"disambiguationData":[OSD([subQ1,subQ0])]}),makeQuery(id+"F1.opExtrude","CAP_EDGE",EDGE,{"disambiguationData":[OSD([subQ1])],"isStart":true})],"blendedInto":[]}),makeQuery(id+"F1.opExtrude","CAP_EDGE",EDGE,{"disambiguationData":[OSD([subQ0])],"isStart":true})],"blendedInto":[]});}
            var Q51;
            {var subQ0=sQuery(id+"F0.wireOp",EDGE,"E9");Q51=makeQuery(id+"F9.opFillet","BLEND_EDGE",EDGE,{"blendedFrom":[makeQuery(id+"F1.opExtrude","SWEPT_EDGE",EDGE,{"disambiguationData":[OSD([sQuery(id+"F0.wireOp",EDGE,"E8"),subQ0])]}),makeQuery(id+"F1.opExtrude","SWEPT_FACE",FACE,{"disambiguationData":[OSD([subQ0])]})],"blendedInto":[makeQuery(id+"F1.opExtrude","SWEPT_FACE",FACE,{"disambiguationData":[OSD([subQ0])]})]});}
            var Q52;
            {var subQ0=sQuery(id+"F0.wireOp",EDGE,"E8");Q52=makeQuery(id+"F9.opFillet","BLEND_EDGE",EDGE,{"blendedFrom":[makeQuery(id+"F1.opExtrude","SWEPT_EDGE",EDGE,{"disambiguationData":[OSD([subQ0,sQuery(id+"F0.wireOp",EDGE,"E9")])]}),makeQuery(id+"F1.opExtrude","SWEPT_FACE",FACE,{"disambiguationData":[OSD([subQ0])]})],"blendedInto":[makeQuery(id+"F1.opExtrude","SWEPT_FACE",FACE,{"disambiguationData":[OSD([subQ0])]})]});}
            var Q53;
            {var subQ0=sQuery(id+"F0.wireOp",EDGE,"E13");var subQ1=sQuery(id+"F0.wireOp",EDGE,"E8");Q53=makeQuery(id+"F10.opFillet","BLEND_EDGE",EDGE,{"blendedFrom":[makeQuery(id+"F1.opExtrude","SWEPT_EDGE",EDGE,{"disambiguationData":[OSD([subQ1,subQ0])]}),makeQuery(id+"F1.opExtrude","SWEPT_FACE",FACE,{"disambiguationData":[OSD([subQ0]),TDD([makeQuery(id+"F0.imprint","IMPRINT",EDGE,{"disambiguationData":[TD([[makeQuery(id+"F0.imprint","INTERSECT",VERTEX,{"derivedFrom":[subQ1,subQ0]}),-1.0]])],"derivedFrom":subQ0})])]})],"blendedInto":[makeQuery(id+"F1.opExtrude","SWEPT_FACE",FACE,{"disambiguationData":[OSD([subQ0]),TDD([makeQuery(id+"F0.imprint","IMPRINT",EDGE,{"disambiguationData":[TD([[makeQuery(id+"F0.imprint","INTERSECT",VERTEX,{"derivedFrom":[subQ1,subQ0]}),-1.0]])],"derivedFrom":subQ0})])]})]});}
            var Q54;
            {var subQ0=sQuery(id+"F0.wireOp",EDGE,"E8");var subQ1=makeQuery(id+"F1.opExtrude","CAP_EDGE",EDGE,{"disambiguationData":[OSD([subQ0])],"isStart":false});var subQ2=sQuery(id+"F0.wireOp",EDGE,"E13");Q54=makeQuery(id+"F10.opFillet","BLEND_EDGE",EDGE,{"blendedFrom":[makeQuery(id+"F9.opFillet","BLEND_EDGE",EDGE,{"blendedFrom":[subQ1,makeQuery(id+"F1.opExtrude","SWEPT_FACE",FACE,{"disambiguationData":[OSD([subQ2]),TDD([makeQuery(id+"F0.imprint","IMPRINT",EDGE,{"disambiguationData":[TD([[makeQuery(id+"F0.imprint","INTERSECT",VERTEX,{"derivedFrom":[subQ0,subQ2]}),-1.0]])],"derivedFrom":subQ2})])]})],"blendedInto":[makeQuery(id+"F1.opExtrude","SWEPT_FACE",FACE,{"disambiguationData":[OSD([subQ2]),TDD([makeQuery(id+"F0.imprint","IMPRINT",EDGE,{"disambiguationData":[TD([[makeQuery(id+"F0.imprint","INTERSECT",VERTEX,{"derivedFrom":[subQ0,subQ2]}),-1.0]])],"derivedFrom":subQ2})])]})]}),makeQuery(id+"F9.opFillet","BLEND_FACE",FACE,{"disambiguationData":[OSD([subQ0]),TDD([subQ1])]})],"blendedInto":[makeQuery(id+"F9.opFillet","BLEND_FACE",FACE,{"disambiguationData":[OSD([subQ0]),TDD([subQ1])]})]});}
            var Q55;
            {var subQ0=sQuery(id+"F0.wireOp",EDGE,"E8");Q55=makeQuery(id+"F9.opFillet","BLEND_EDGE",EDGE,{"blendedFrom":[makeQuery(id+"F1.opExtrude","CAP_EDGE",EDGE,{"disambiguationData":[OSD([subQ0])],"isStart":false}),makeQuery(id+"F1.opExtrude","SWEPT_FACE",FACE,{"disambiguationData":[OSD([subQ0])]})],"blendedInto":[makeQuery(id+"F1.opExtrude","SWEPT_FACE",FACE,{"disambiguationData":[OSD([subQ0])]})]});}
            var Q56;
            {var subQ0=sQuery(id+"F0.wireOp",EDGE,"E8");var subQ1=makeQuery(id+"F1.opExtrude","CAP_EDGE",EDGE,{"disambiguationData":[OSD([subQ0])],"isStart":false});Q56=makeQuery(id+"F10.opFillet","BLEND_EDGE",EDGE,{"blendedFrom":[makeQuery(id+"F9.opFillet","BLEND_EDGE",EDGE,{"blendedFrom":[makeQuery(id+"F1.opExtrude","SWEPT_EDGE",EDGE,{"disambiguationData":[OSD([subQ0,sQuery(id+"F0.wireOp",EDGE,"E9")])]}),subQ1],"blendedInto":[]}),makeQuery(id+"F9.opFillet","BLEND_FACE",FACE,{"disambiguationData":[OSD([subQ0]),TDD([subQ1])]})],"blendedInto":[makeQuery(id+"F9.opFillet","BLEND_FACE",FACE,{"disambiguationData":[OSD([subQ0]),TDD([subQ1])]})]});}
            var Q57;
            {var subQ0=sQuery(id+"F0.wireOp",EDGE,"E8");Q57=makeQuery(id+"F9.opFillet","BLEND_EDGE",EDGE,{"blendedFrom":[makeQuery(id+"F1.opExtrude","CAP_EDGE",EDGE,{"disambiguationData":[OSD([subQ0])],"isStart":false}),makeQuery(id+"F1.opExtrude","CAP_FACE",FACE,{"disambiguationData":[OSD([sQuery(id+"F0.wireOp",EDGE,"E0"),sQuery(id+"F0.wireOp",EDGE,"E1"),sQuery(id+"F0.wireOp",EDGE,"E7"),subQ0,sQuery(id+"F0.wireOp",EDGE,"E9"),sQuery(id+"F0.wireOp",EDGE,"E11"),sQuery(id+"F0.wireOp",EDGE,"E12"),sQuery(id+"F0.wireOp",EDGE,"E13"),sQuery(id+"F0.wireOp",EDGE,"E14")])],"isStart":false})],"blendedInto":[makeQuery(id+"F1.opExtrude","CAP_FACE",FACE,{"disambiguationData":[OSD([sQuery(id+"F0.wireOp",EDGE,"E0"),sQuery(id+"F0.wireOp",EDGE,"E1"),sQuery(id+"F0.wireOp",EDGE,"E7"),subQ0,sQuery(id+"F0.wireOp",EDGE,"E9"),sQuery(id+"F0.wireOp",EDGE,"E11"),sQuery(id+"F0.wireOp",EDGE,"E12"),sQuery(id+"F0.wireOp",EDGE,"E13"),sQuery(id+"F0.wireOp",EDGE,"E14")])],"isStart":false})]});}
            var Q58;
            {var subQ0=sQuery(id+"F0.wireOp",EDGE,"E9");var subQ1=sQuery(id+"F0.wireOp",EDGE,"E8");Q58=makeQuery(id+"F10.opFillet","BLEND_EDGE",EDGE,{"blendedFrom":[makeQuery(id+"F9.opFillet","BLEND_EDGE",EDGE,{"blendedFrom":[makeQuery(id+"F1.opExtrude","SWEPT_EDGE",EDGE,{"disambiguationData":[OSD([subQ1,subQ0])]}),makeQuery(id+"F1.opExtrude","CAP_EDGE",EDGE,{"disambiguationData":[OSD([subQ1])],"isStart":false})],"blendedInto":[]}),makeQuery(id+"F1.opExtrude","CAP_EDGE",EDGE,{"disambiguationData":[OSD([subQ0])],"isStart":false})],"blendedInto":[]});}
            var Q59;
            {var subQ0=sQuery(id+"F0.wireOp",EDGE,"E9");Q59=makeQuery(id+"F10.opFillet","BLEND_EDGE",EDGE,{"blendedFrom":[makeQuery(id+"F1.opExtrude","CAP_EDGE",EDGE,{"disambiguationData":[OSD([subQ0])],"isStart":false}),makeQuery(id+"F1.opExtrude","SWEPT_FACE",FACE,{"disambiguationData":[OSD([subQ0])]})],"blendedInto":[makeQuery(id+"F1.opExtrude","SWEPT_FACE",FACE,{"disambiguationData":[OSD([subQ0])]})]});}
            var Q60;
            Q60=makeQuery(id+"F1.opExtrude","CAP_EDGE",EDGE,{"disambiguationData":[OSD([sQuery(id+"F0.wireOp",EDGE,"E1")])],"isStart":false});
            var Q61;
            {var subQ0=sQuery(id+"F0.wireOp",EDGE,"E1");var subQ1=sQuery(id+"F0.wireOp",EDGE,"E13");Q61=makeQuery(id+"F10.opFillet","BLEND_EDGE",EDGE,{"blendedFrom":[makeQuery(id+"F1.opExtrude","CAP_EDGE",EDGE,{"disambiguationData":[OSD([subQ1]),TDD([makeQuery(id+"F0.imprint","IMPRINT",EDGE,{"disambiguationData":[TD([[makeQuery(id+"F0.imprint","INTERSECT",VERTEX,{"derivedFrom":[sQuery(id+"F0.wireOp",EDGE,"E8"),subQ1]}),-1.0]])],"derivedFrom":subQ1})])],"isStart":false}),makeQuery(id+"F1.opExtrude","SWEPT_FACE",FACE,{"disambiguationData":[OSD([subQ0])]})],"blendedInto":[makeQuery(id+"F1.opExtrude","SWEPT_FACE",FACE,{"disambiguationData":[OSD([subQ0])]})]});}
            var Q62;
            Q62=makeQuery(id+"F1.opExtrude","SWEPT_EDGE",EDGE,{"disambiguationData":[OSD([sQuery(id+"F0.wireOp",EDGE,"E9"),sQuery(id+"F0.wireOp",EDGE,"E11")])]});
            fillet(context, id + "F11", {"entities" : qUnion([Q0, Q1, Q2, Q3, Q4, Q5, Q6, Q7, Q8, Q9, Q10, Q11, Q12, Q13, Q14, Q15, Q16, Q17, Q18, Q19, Q20, Q21, Q22, Q23, Q24, Q25, Q26, Q27, Q28, Q29, Q30, Q31, Q32, Q33, Q34, Q35, Q36, Q37, Q38, Q39, Q40, Q41, Q42, Q43, Q44, Q45, Q46, Q47, Q48, Q49, Q50, Q51, Q52, Q53, Q54, Q55, Q56, Q57, Q58, Q59, Q60, Q61, Q62]), "radius" : 1.27 * mm, "tangentPropagation" : true, "allowEdgeOverflow" : false});
        }
    });
